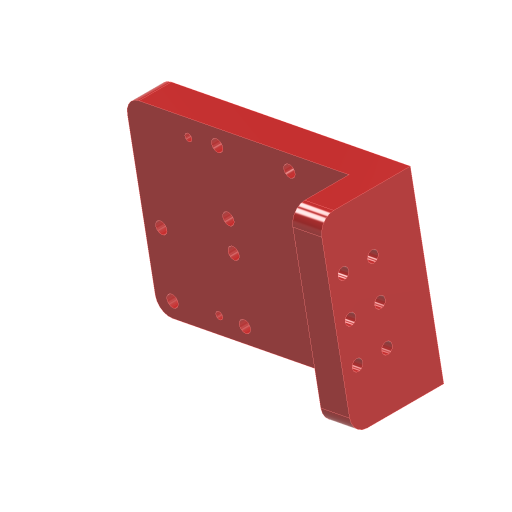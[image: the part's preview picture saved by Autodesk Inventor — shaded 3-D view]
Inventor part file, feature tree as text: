
AUTODESK INVENTOR PART (.ipt)
format: ipt  version: 2024.3 (Build 283343000, 343)  size: 223,232 bytes
history: native  units: mm
features: reference x8, sketch x7, other x7, hole x5, extrude x2, projected_geometry x2, direct_edit x1, fillet x1, chamfer x1, move_body x1
ambient origin geometry x8: Origin, YZ Plane, XZ Plane, XY Plane, X Axis, Y Axis, Z Axis, Center Point
bodies: Solid1 (feature_tree)
feature tree (35):
  extrude  "Extrusion1"  Depth=3.0mm
  hole  "Hole1"  [1 undecoded]
  hole  "Hole2"  [1 undecoded]
  extrude  "Extrusion2"  TaperAngle=0.0deg  [1 undecoded]
  hole  "Hole3"  [1 undecoded]
  direct_edit  "Direct Edit1"
  fillet  "Fillet1"  Radius=25.0mm
  hole  "Hole4"  [1 undecoded]
  hole  "Hole5"  [1 undecoded]
  chamfer  "Chamfer1"  Distance=5.0mm
  sketch  "Sketch1"  dims[d0=3.0mm d1=12.0mm]
  reference  "Reference1"
  reference  "Reference2"
  reference  "Reference3"
  reference  "Reference4"
  reference  "Reference5"
  reference  "Reference6"
  reference  "Reference7"
  reference  "Reference8"
  sketch  "Sketch2"  dims[d2=11.0mm d3=0.0mm]
  sketch  "Sketch3"  dims[d4=2.4mm d5=6.0mm d6=4.4mm d7=2.0mm d8=90.0deg d9=8.0mm d10=20.594885mm]
  sketch  "Sketch4"  dims[d11=3.6mm d12=6.0mm d13=4.0mm d14=2.0mm d15=90.0deg d16=3.0mm d17=0.0mm d18=10.0mm]
  projected_geometry  "Projected Loop1"
  sketch  "Sketch5"  dims[d19=20.0mm d20=0.0mm d21=25.0mm]
  projected_geometry  "Projected Loop2"
  sketch  "Sketch6"  dims[d22=10.0mm]
  sketch  "Sketch7"  dims[d23=3.6mm d24=6.0mm d25=6.3mm d26=2.0mm d27=90.0deg d28=3.0mm d29=0.0mm d30=0.0mm d31=0.0mm d32=-5.0mm d33=5.0mm d34=2.6mm d35=6.0mm d36=4.4mm d37=2.0mm d38=90.0deg d39=8.0mm d40=20.594885mm d41=3.9mm d42=6.0mm d43=4.0mm d44=2.0mm d45=90.0deg d46=3.0mm d47=0.0mm d49=25.0mm d50=20.0mm d51=17.0mm d52=5.0mm d54=20.0mm d55=25.0mm d56=5.0mm d57=6.0mm d58=0.6mm d59=2.0mm d60=45.0deg]
  parser-record x1  (decoder bookkeeping rows leaked as tree rows — omitted from the tree; the rows remain in map.json)
  other  "Arduino_zlozenie.iam"
  other  "Arduino-cz1:2"
  other  "Arduino-cz1:1"
  other  "Arduino-cz1:4"
  other  "Arduino-cz1:3"
  other  "Arduino UNO Wifi:1"
  move_body  "Move1"
note: 6 required parameter values undecoded (feature->parameter linkage not recoverable at this tier; creation-order binding heuristic only, values carry confidence <= 0.55)
note: 1 file-system path scrubbed to <path> (originals preserved in map.json)
